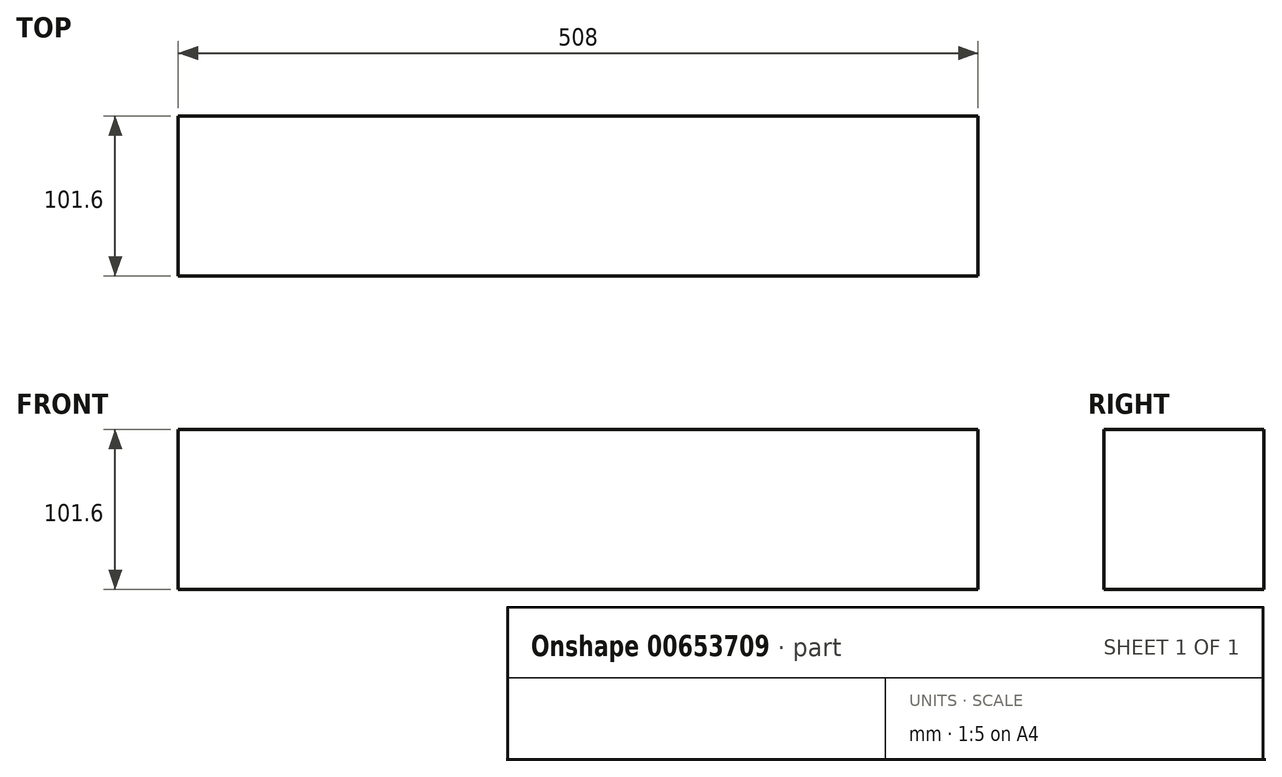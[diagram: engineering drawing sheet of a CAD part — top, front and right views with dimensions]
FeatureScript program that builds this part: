
annotation { "Feature Type Name" : "Feature", "Feature Type Description" : "" }
export const myFeature = defineFeature(function(context is Context, id is Id, definition is map)
    precondition{}
    {
        {
            var Q0;
            Q0=qCreatedBy(makeId("Right.planeOp"),FACE);
            var sketch = newSketch(context, id + "F0", { "sketchPlane" : qUnion([Q0])});
            skLineSegment(sketch, "E0.bottom", {"start": v(-46.88, 58.52) * mm, "end": v(54.72, 58.52) * mm});
            skLineSegment(sketch, "E0.top", {"start": v(-46.88, -43.08) * mm, "end": v(54.72, -43.08) * mm});
            skLineSegment(sketch, "E0.left", {"start": v(-46.88, 58.52) * mm, "end": v(-46.88, -43.08) * mm});
            skLineSegment(sketch, "E0.right", {"start": v(54.72, 58.52) * mm, "end": v(54.72, -43.08) * mm});
            skSolve(sketch);
        }
        {
            var Q0;
            Q0=makeQuery(id+"F0.imprint","IMPRINT",FACE,{"disambiguationData":[TD([[makeQuery(id+"F0.imprint","IMPRINT",EDGE,{"derivedFrom":sQuery(id+"F0.wireOp",EDGE,"E0.bottom")}),-1.0]])]});
            extrude(context, id + "F1", {"entities" : qUnion([Q0]), "depth" : 508 * mm, "offsetDistance" : 25.4 * mm});
        }
    });
